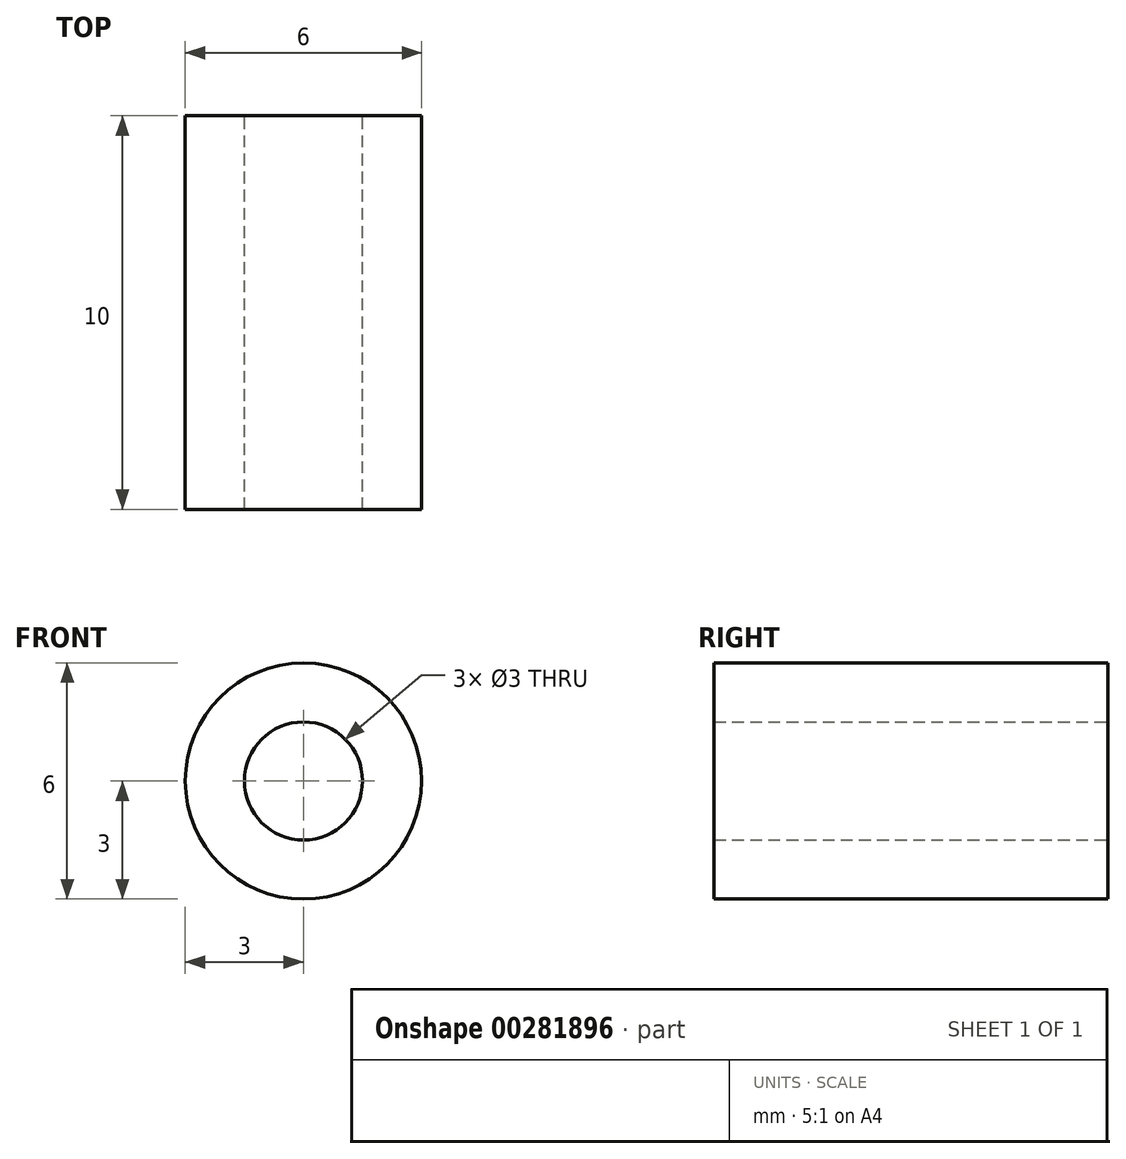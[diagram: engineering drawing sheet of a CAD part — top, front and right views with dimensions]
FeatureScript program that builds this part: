
annotation { "Feature Type Name" : "Feature", "Feature Type Description" : "" }
export const myFeature = defineFeature(function(context is Context, id is Id, definition is map)
    precondition{}
    {
        {
            var Q0;
            Q0=qCreatedBy(makeId("Front.planeOp"),FACE);
            var sketch = newSketch(context, id + "F0", { "sketchPlane" : qUnion([Q0])});
            skCircle(sketch, "E0", {"center": v(0, 0) * mm, "radius": 1.5 * mm});
            skCircle(sketch, "E1", {"center": v(0, 0) * mm, "radius": 3 * mm});
            skSolve(sketch);
        }
        {
            var Q0;
            Q0=qSketchRegion(id+"F0",true);
            extrude(context, id + "F1", {"entities" : qUnion([Q0]), "depth" : 10 * mm});
        }
    });
